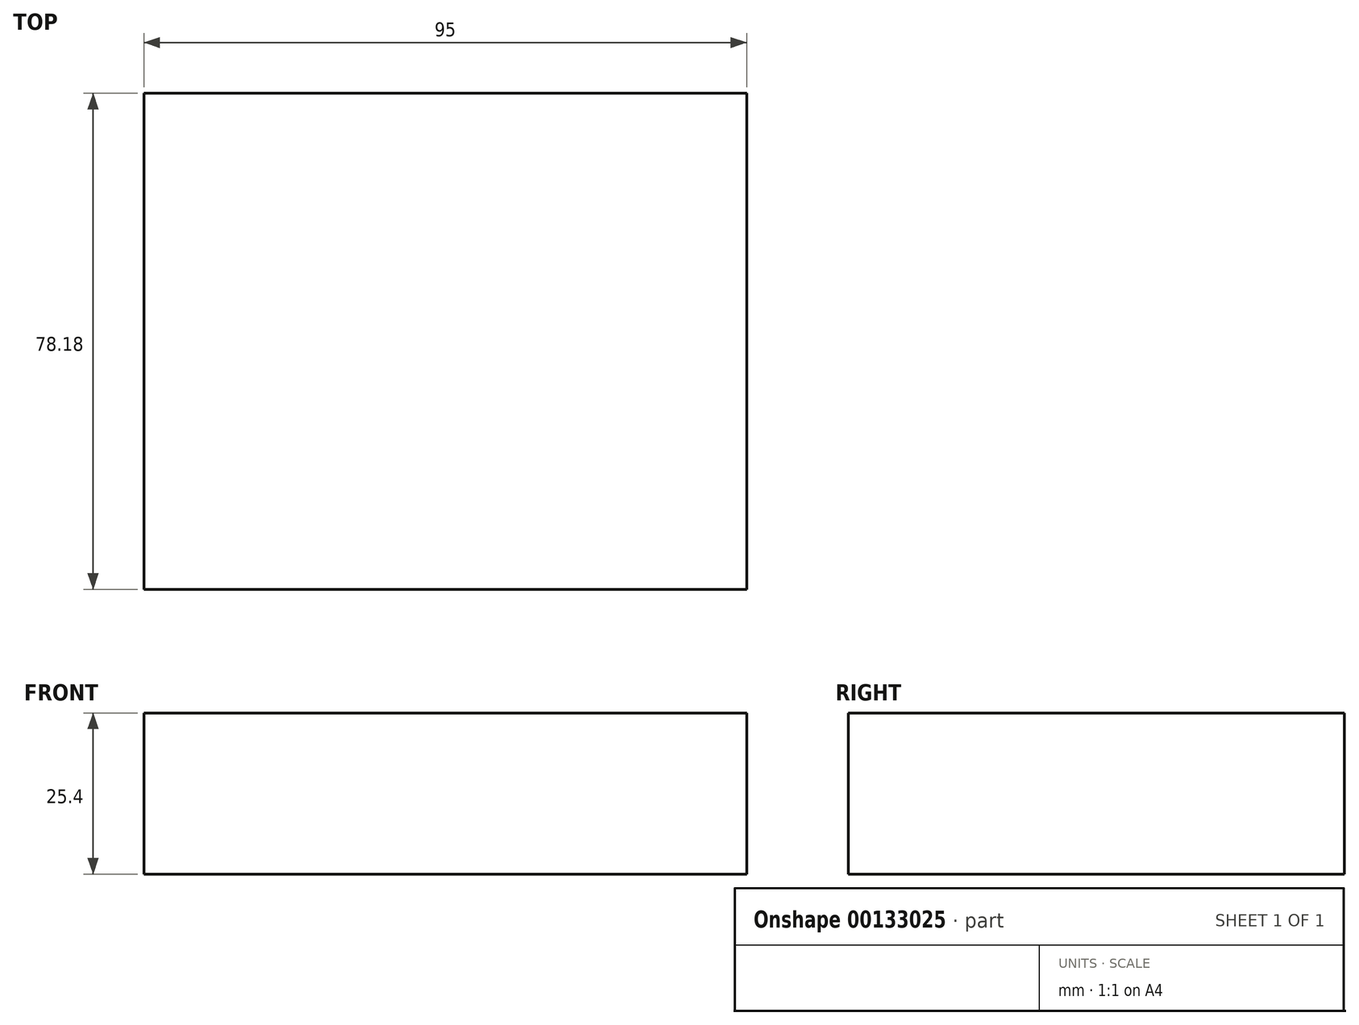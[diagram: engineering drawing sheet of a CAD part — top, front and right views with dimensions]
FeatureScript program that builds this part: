
annotation { "Feature Type Name" : "Feature", "Feature Type Description" : "" }
export const myFeature = defineFeature(function(context is Context, id is Id, definition is map)
    precondition{}
    {
        {
            var Q0;
            Q0=qCreatedBy(makeId("Top.planeOp"),FACE);
            var sketch = newSketch(context, id + "F0", { "sketchPlane" : qUnion([Q0])});
            skLineSegment(sketch, "E0.bottom", {"start": v(-45.4, 39.37) * mm, "end": v(49.6, 39.37) * mm});
            skLineSegment(sketch, "E0.top", {"start": v(-45.4, -38.81) * mm, "end": v(49.6, -38.81) * mm});
            skLineSegment(sketch, "E0.left", {"start": v(-45.4, 39.37) * mm, "end": v(-45.4, -38.81) * mm});
            skLineSegment(sketch, "E0.right", {"start": v(49.6, 39.37) * mm, "end": v(49.6, -38.81) * mm});
            skSolve(sketch);
        }
        {
            var Q0;
            Q0 = qSketchRegion(id + "F0", true);
            extrude(context, id + "F1", {"entities" : qUnion([Q0]), "depth" : 25.4 * mm});
        }
    });
